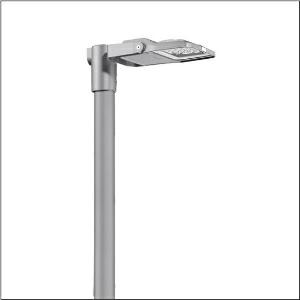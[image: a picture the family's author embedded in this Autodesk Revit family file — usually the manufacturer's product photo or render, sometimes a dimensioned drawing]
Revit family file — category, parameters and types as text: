
# Revit family: floodlight_fl_21_iq_micro___pl33t_5xa7761a4f3a_749b
name_source: partatom
category: Lighting Fixtures
units: mm (PartAtom-declared; Revit-internal decimal feet)

## family parameters
Cut with Voids When Loaded = No
Host = Face
Light Source = No
Part Type = Normal
Room Calculation Point = No
Round Connector Dimension = Use Diameter
Shared = No

## types (1)
- --- (1 x LED, 3050 lm, 23.1 W, 4000K)
    Apparent Load = 23 VA
    CIE Flux Codes = 26 75 99 100 100
    Color Rendering = 70
    Color Temperature = 4000K
    Default Elevation = 1800 mm
    Description = Floodlight FL 21 iQ micro, floodlight, primary light control with lens, of PMMA, primary optical cover: protective disc, of toughened safety glass, transparent, light distribution: PL33T, light emission: direct distribution, installation type: surface-mounted, lamps: LED, High Power LED, rated values: 3.050lm | 23,1W | 132lm/W (begin service life); end service life: 3.050lm | 23,8W; at 50% lumin. flux: 1.525lm | 11W | 138,6lm/W, colour temperature: 4000K, colour rendering: CRI > 70, light colour: 740, light setting 1 begin service life: 100% | 3.050lm | 23,1W | 132lm/W | 4.000K, light setting 1 end service life: 23,8W, further light settings possible, control: optimised constant luminous flux control (CLO 2.0), Desk-Remote (wireless, voltage-free reading and setting of iQ features in the workshop via application-optimized NFC function/RFID function), Light-Fading, Smart-Wire, Night-Set, Lumen-Switch, Temp-Guard, Auto-Match, pre-setting: linear dimming characteristic, with terminal, 6-pole, mains connection: 220..240V, AC, 50/60Hz, luminaire housing, of diecast aluminium, powder-coated, SITECO metallic grey (DB 702S), corrosivity category C5 mid according to DIN EN ISO 12944suitable for swimming poolschlorine-resistant, sealing non-destructively replaceable, please order mast flange separately, mast bracket, of steel, galvanised, powder-coated, SITECO metallic grey (DB 702S), protection rating (complete): IP66, insulation class (complete): insulation class II (safety insulation), certification: CE, ENEC, VDE, protection symbol: D, impact resistance: IK07, permissible operating ambient temperature: -40..+40°C, permissible operating ambient temperature for outdoor applications: -40..+50°C, standard: DIN EN 12944, LABS conformity tested according to VDMA 24364:2018-05, packaging unit: 1 piece

Light Distribution: PL33T
    Height = 65 mm
    Lamp = 1 x LED
    Lamp Light Flux = 3050 lm
    Lamp Power = 23.1 W
    Lamp count = 1
    Length = 312 mm
    Luminous efficacy = 132 lm/W
    Manufacturer = Siteco
    ModVariant = No
    Model = 5XA7761A4F3A
    Mounting Place = Pole
    Mounting Type = Pole annexe
    Number of Poles = 1
    OnlyDefault = Yes
    Power Factor = 1
    Product Name = Floodlight FL 21 iQ micro | PL33T
    Product group = floodlight | pylon annexe
    ProductGroupID = 6201
    Protection Class = Protection class II
    Protection Degree = IP 66
    RLX_Detail_Level = 1
    RLX_Emergency_Light_Flux = 0 lm
    RLX_Emergency_Type = 0
    RLX_Emergency_Type_DB = No
    RlxData = <blob elided: 102005 chars, md5=31ef797d>
    Socket = socket
    Standby Power = 0 W
    System Light Flux = 3050 lm
    System Power = 23 W
    Type Comments = factory setting: luminous flux: 100 % | dim-lin: 254 | 455 mA
    Type Image = l_1007121.jpg
    URL = http://relux.com
    VarID = @adj_149161
    Voltage = 0 V
    Weight = 0.00 kg
    Width = 230 mm

## geometry (parser evidence)
native form markers: Blend x4, Sweep x12
no freeform markers — native parametric forms only
